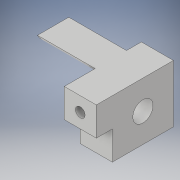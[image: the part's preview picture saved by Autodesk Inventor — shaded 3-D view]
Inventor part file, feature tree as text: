
AUTODESK INVENTOR PART (.ipt)
format: ipt  version: 2019 (Build 230136000, 136)  size: 143,872 bytes
history: native  units: in
note: dims shown in document units (in); Inventor stores cm internally (conversion verified against a paired STEP export)
features: sketch x5, extrude x4, hole x1
ambient origin geometry x8: Origin, YZ Plane, XZ Plane, XY Plane, X Axis, Y Axis, Z Axis, Center Point
bodies: Solid1 (feature_tree)
feature tree (10):
  sketch  "Sketch1"  dims[d0=0.4488in d1=0.4764in]
  extrude  "Extrusion1"  Depth=0.4764in
  extrude  "Extrusion2"  Depth=0.1162in
  sketch  "Sketch3"  dims[d2=0.244in d3=0.1162in]
  sketch  "Sketch6"  dims[d4=0.25in d5=0.0in d6=0.45in d7=0.0in]
  hole  "Hole2"  [1 undecoded]
  extrude  "Extrusion8"  Depth=0.4764in
  sketch  "Sketch7"  dims[d19=0.4764in d20=0.2382in]
  extrude  "Extrusion9"  Depth=0.4488in
  sketch  "Sketch8"  dims[d29=0.0787in d30=0.4488in d31=0.2244in d33=0.4488in d37=0.1575in d38=0.75in d39=0.119in d40=0.25in d41=0.5635in d42=1.0in d43=0.8108in d46=0.2244in d47=0.125in d48=0.0in d50=0.25in d51=0.2244in d52=0.1122in d53=0.125in d63=0.1122in d64=0.125in d65=0.075in d66=0.35in d67=0.0in d54=1.0in d55=1.0in d56=1.0in d57=0.15in d58=0.25in d59=0.375in d60=0.5635in d61=0.75in d62=0.8108in]
note: 1 required parameter value undecoded (feature->parameter linkage not recoverable at this tier; creation-order binding heuristic only, values carry confidence <= 0.55)
